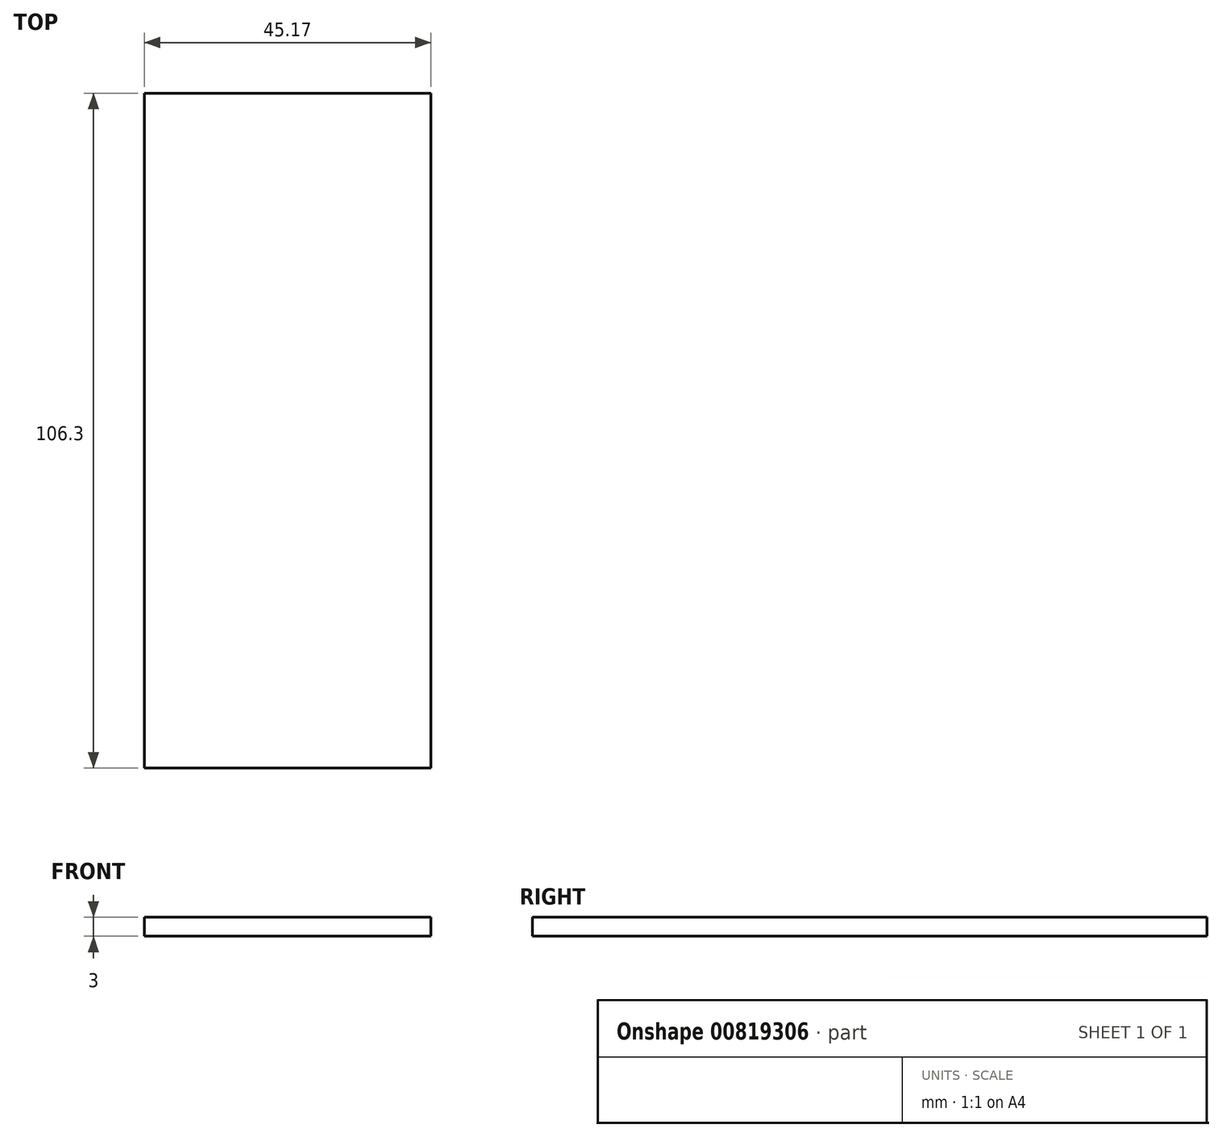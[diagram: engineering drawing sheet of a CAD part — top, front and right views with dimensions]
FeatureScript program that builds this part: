
annotation { "Feature Type Name" : "Feature", "Feature Type Description" : "" }
export const myFeature = defineFeature(function(context is Context, id is Id, definition is map)
    precondition{}
    {
        {
            var Q0;
            Q0=qCreatedBy(makeId("Top.planeOp"),FACE);
            var sketch = newSketch(context, id + "F0", { "sketchPlane" : qUnion([Q0])});
            skLineSegment(sketch, "E0.bottom", {"start": v(0, 106.3) * mm, "end": v(45.17, 106.3) * mm});
            skLineSegment(sketch, "E0.top", {"start": v(0, 0) * mm, "end": v(45.17, 0) * mm});
            skLineSegment(sketch, "E0.left", {"start": v(0, 106.3) * mm, "end": v(0, 0) * mm});
            skLineSegment(sketch, "E0.right", {"start": v(45.17, 106.3) * mm, "end": v(45.17, 0) * mm});
            skSolve(sketch);
        }
        {
            var Q0;
            Q0=makeQuery(id+"F0.imprint","IMPRINT",FACE,{"disambiguationData":[TD([[makeQuery(id+"F0.imprint","IMPRINT",EDGE,{"derivedFrom":sQuery(id+"F0.wireOp",EDGE,"E0.bottom")}),-1.0]])]});
            var sketch = newSketch(context, id + "F1", { "sketchPlane" : qUnion([Q0])});
            skSolve(sketch);
        }
        {
            var Q0;
            Q0=makeQuery(id+"F0.imprint","IMPRINT",FACE,{"disambiguationData":[TD([[makeQuery(id+"F0.imprint","IMPRINT",EDGE,{"derivedFrom":sQuery(id+"F0.wireOp",EDGE,"E0.bottom")}),-1.0]])]});
            extrude(context, id + "F2", {"entities" : qUnion([Q0]), "depth" : 3 * mm, "offsetDistance" : 25.4 * mm});
        }
        {
            var Q0;
            Q0=makeQuery(id+"F2.opExtrude","CAP_FACE",FACE,{"disambiguationData":[OSD([sQuery(id+"F0.wireOp",EDGE,"E0.bottom"),sQuery(id+"F0.wireOp",EDGE,"E0.top"),sQuery(id+"F0.wireOp",EDGE,"E0.left"),sQuery(id+"F0.wireOp",EDGE,"E0.right")])],"isStart":false});
            var sketch = newSketch(context, id + "F3", { "sketchPlane" : qUnion([Q0])});
            skSolve(sketch);
        }
        {
            var Q0;
            Q0=makeQuery(id+"F3.imprint","IMPRINT",FACE,{"disambiguationData":[TD([[makeQuery(id+"F3.imprint","IMPRINT",EDGE,{"derivedFrom":makeQuery(id+"F2.opExtrude","CAP_EDGE",EDGE,{"disambiguationData":[OSD([sQuery(id+"F0.wireOp",EDGE,"E0.bottom")])],"isStart":false})}),-1.0]])]});
            var sketch = newSketch(context, id + "F4", { "sketchPlane" : qUnion([Q0])});
            skArc(sketch, "E1", {"start": v(36.64, 105.26) * mm, "mid": v(25.15, 132.34) * mm, "end": v(9.6, 107.37) * mm});
            skSolve(sketch);
        }
        {
            var Q0;
            Q0=sQuery(id+"F4.wireOp",EDGE,"E1");
            extrude(context, id + "F5", {"bodyType" : ToolBodyType.SURFACE, "surfaceEntities" : qUnion([Q0]), "depth" : 3 * mm, "offsetDistance" : 25 * mm});
        }
        {
            var Q0;
            Q0=qCreatedBy(makeId("Top.planeOp"),FACE);
            var sketch = newSketch(context, id + "F6", { "sketchPlane" : qUnion([Q0])});
            skArc(sketch, "E2", {"start": v(45.96, 46.07) * mm, "mid": v(68.67, 57.62) * mm, "end": v(44.74, 66.37) * mm});
            skArc(sketch, "E3", {"start": v(10.14, 0) * mm, "mid": v(18.1, -14.9) * mm, "end": v(26.05, 0) * mm});
            skSolve(sketch);
        }
        {
            var Q0;
            Q0=sQuery(id+"F6.wireOp",EDGE,"E2");
            extrude(context, id + "F7", {"bodyType" : ToolBodyType.SURFACE, "surfaceEntities" : qUnion([Q0]), "depth" : 3 * mm, "offsetDistance" : 25 * mm});
        }
        {
            var Q0;
            Q0=qCreatedBy(makeId("Top.planeOp"),FACE);
            var sketch = newSketch(context, id + "F8", { "sketchPlane" : qUnion([Q0])});
            skArc(sketch, "E4", {"start": v(8.55, 0) * mm, "mid": v(16.64, -16.06) * mm, "end": v(24.73, 0) * mm});
            skSolve(sketch);
        }
        {
            var Q0;
            Q0=sQuery(id+"F8.wireOp",EDGE,"E4");
            extrude(context, id + "F9", {"bodyType" : ToolBodyType.SURFACE, "surfaceEntities" : qUnion([Q0]), "depth" : 3 * mm, "offsetDistance" : 25 * mm});
        }
    });
